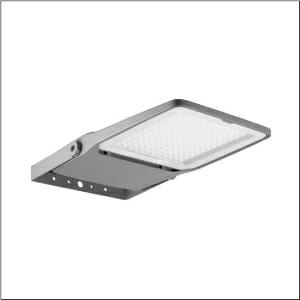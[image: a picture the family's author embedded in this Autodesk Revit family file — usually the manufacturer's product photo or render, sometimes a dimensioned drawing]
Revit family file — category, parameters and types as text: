
# Revit family: floodlight_fl_20_midi___rs05_5xa7682g3h2ac_e142
name_source: partatom
category: Lighting Fixtures
units: mm (PartAtom-declared; Revit-internal decimal feet)

## family parameters
Cut with Voids When Loaded = No
Host = Face
Light Source = No
Part Type = Normal
Room Calculation Point = No
Round Connector Dimension = Use Diameter
Shared = No

## types (1)
- --- (1 x LED 5000K / CRI = 70 (unbekannt), 39000 lm, 5000K)
    Apparent Load = 306 VA
    CIE Flux Codes = 81 94 99 100 100
    Color Rendering = 70
    Color Temperature = 5000K
    Default Elevation = 1800 mm
    Description = Floodlight FL 20 midi, floodlight, primary light control with lens, of plastic, primary optical cover: protective disc, of toughened safety glass, transparent, light distribution: RS05, light emission: direct distribution, primary light characteristic: rotationally symmetric, installation type: surface-mounted, LED, High Power LED, rated luminous flux: 39.000lm, luminous efficacy: 128lm/W, light colour: 750, colour temperature: 5000K, control gear: ECG Plus, control: overheat protection, power reduction, digital communication interface, time-dependent luminous flux control, flexible luminous flux parameterisation, electronic power reduction, with terminal, 10-pole, max. 2.5mm², mains connection: 220..240V, AC, 50/60Hz, rated input power: 306W, LED unit, of diecast aluminium, powder-coated, Siteco® metallic grey (DB 702S), corrosivity category C5 mid according to DIN EN ISO 12944, length: 731mm, width: 450mm, height: 76mm, housing frame, of diecast aluminium, powder-coated, Siteco® metallic grey (DB 702S), wall fastening, DALI, protection rating (complete): IP66, insulation class (complete): insulation class II (safety insulation), certification: CE, ENEC, VDE, protection symbol: D, permissible operating ambient temperature: -40..+40°C, permissible operating ambient temperature for outdoor applications: -40..+50°C, standard: DIN EN 12944, packaging unit: 1 piece

Light Distribution: RS05
    Height = 76 mm
    Lamp = 1 x LED 5000K / CRI >= 70 (unbekannt)
    Lamp Light Flux = 39000 lm
    Lamp count = 1
    Length = 731 mm
    Luminous efficacy = 128 lm/W
    Manufacturer = Siteco
    ModVariant = No
    Model = 5XA7682G3H2AC
    Number of Poles = 1
    OnlyDefault = Yes
    Power Factor = 1
    Product Name = Floodlight FL 20 midi | RS05
    Product group = floodlight | pylon annexe
    ProductGroupID = 6200
    Protection Class = Protection class II
    Protection Degree = IP 66
    RLX_Detail_Level = 1
    RLX_Emergency_Light_Flux = 0 lm
    RLX_Emergency_Type = 0
    RLX_Emergency_Type_DB = No
    RlxData = <blob elided: 86613 chars, md5=83520dc4>
    Socket = socket
    Standby Power = 0 W
    System Light Flux = 39000 lm
    System Power = 306 W
    Type Comments = factory setting: luminous flux: 100 % | dim-lin: 254 | 700 mA
    Type Image = l_1005944.jpg
    URL = http://relux.com
    VarID = @adj_146269
    Voltage = 0 V
    Weight = 0.00 kg
    Width = 450 mm

## geometry (parser evidence)
native form markers: Blend x4, Sweep x13
no freeform markers — native parametric forms only
